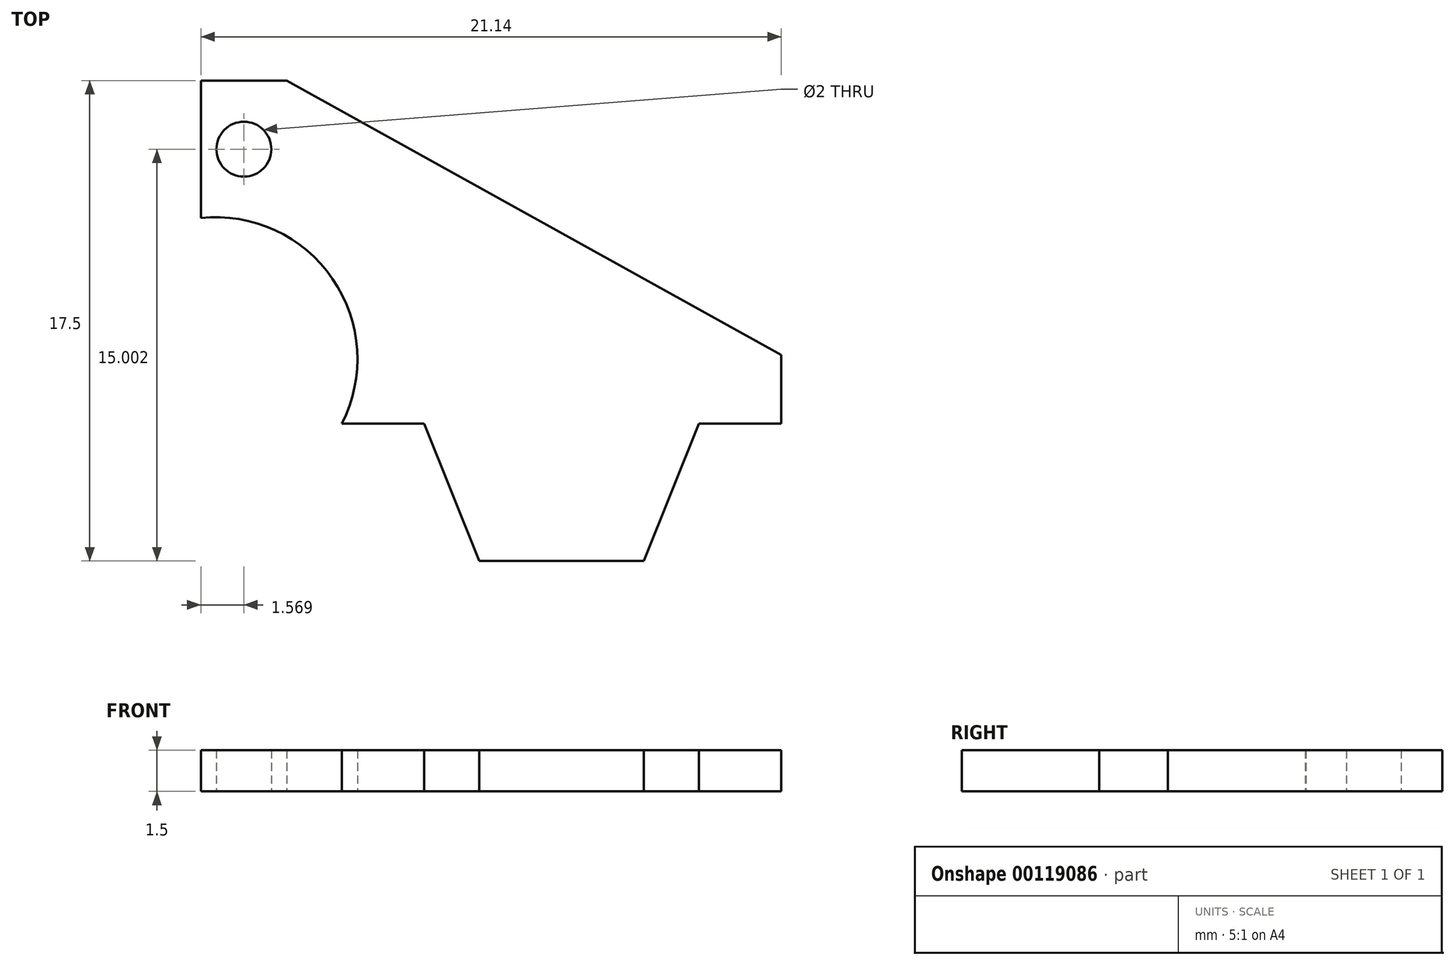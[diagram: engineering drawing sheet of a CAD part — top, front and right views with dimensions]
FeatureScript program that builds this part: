
annotation { "Feature Type Name" : "Feature", "Feature Type Description" : "" }
export const myFeature = defineFeature(function(context is Context, id is Id, definition is map)
    precondition{}
    {
        {
            var Q0;
            Q0=qCreatedBy(makeId("Top.planeOp"),FACE);
            var sketch = newSketch(context, id + "F0", { "sketchPlane" : qUnion([Q0])});
            skLineSegment(sketch, "E0", {"start": v(-58.9, 5.22) * mm, "end": v(-52.9, 5.22) * mm});
            skLineSegment(sketch, "E1", {"start": v(-55.9, 5.22) * mm, "end": v(-55.9, 10.22) * mm});
            skLineSegment(sketch, "E2", {"start": v(-55.9, 10.22) * mm, "end": v(-50.9, 10.22) * mm});
            skLineSegment(sketch, "E3", {"start": v(-55.9, 10.22) * mm, "end": v(-60.9, 10.22) * mm});
            skLineSegment(sketch, "E4", {"start": v(-60.9, 10.22) * mm, "end": v(-58.9, 5.22) * mm});
            skLineSegment(sketch, "E5", {"start": v(-52.9, 5.22) * mm, "end": v(-50.9, 10.22) * mm});
            skLineSegment(sketch, "E6", {"start": v(-60.9, 10.22) * mm, "end": v(-63.9, 10.22) * mm});
            skLineSegment(sketch, "E7", {"start": v(-50.9, 10.22) * mm, "end": v(-47.9, 10.22) * mm});
            skLineSegment(sketch, "E8", {"start": v(-47.9, 10.22) * mm, "end": v(-47.9, 12.72) * mm});
            skLineSegment(sketch, "E9", {"start": v(-58.9, 0) * mm, "end": v(-65.9, 0) * mm});
            skLineSegment(sketch, "E10", {"start": v(-58.9, 5.22) * mm, "end": v(-58.9, 22.72) * mm});
            skLineSegment(sketch, "E11", {"start": v(-65.9, 22.72) * mm, "end": v(-47.9, 12.72) * mm});
            skLineSegment(sketch, "E12", {"start": v(-65.9, 22.72) * mm, "end": v(-69.04, 22.72) * mm});
            skLineSegment(sketch, "E13", {"start": v(-69.04, 22.72) * mm, "end": v(-69.04, 17.72) * mm});
            skArc(sketch, "E14", {"start": v(-63.9, 10.22) * mm, "mid": v(-64.24, 15.5) * mm, "end": v(-69.04, 17.72) * mm});
            skCircle(sketch, "E15", {"center": v(-67.47, 20.22) * mm, "radius": 1 * mm});
            skPoint(sketch, "E15.centerSnap0", {"position": v(-69.04, 20.22) * mm});
            skPoint(sketch, "E15.centerSnap1", {"position": v(-67.47, 22.72) * mm});
            skSolve(sketch);
        }
        {
            var Q0;
            {var subQ6=sQuery(id+"F0.wireOp",EDGE,"E6");Q0=makeQuery(id+"F0.imprint","IMPRINT",FACE,{"disambiguationData":[TD([[makeQuery(id+"F0.imprint","IMPRINT",EDGE,{"derivedFrom":subQ6}),-1.0]])]});}
            var Q1;
            {var subQ1=sQuery(id+"F0.wireOp",EDGE,"E2");Q1=makeQuery(id+"F0.imprint","IMPRINT",FACE,{"disambiguationData":[TD([[makeQuery(id+"F0.imprint","IMPRINT",EDGE,{"derivedFrom":subQ1}),1.0]])]});}
            var Q2;
            {var subQ3=sQuery(id+"F0.wireOp",EDGE,"E1");Q2=makeQuery(id+"F0.imprint","IMPRINT",FACE,{"disambiguationData":[TD([[makeQuery(id+"F0.imprint","IMPRINT",EDGE,{"derivedFrom":subQ3}),1.0]])]});}
            var Q3;
            {var subQ0=sQuery(id+"F0.wireOp",EDGE,"E4");Q3=makeQuery(id+"F0.imprint","IMPRINT",FACE,{"disambiguationData":[TD([[makeQuery(id+"F0.imprint","IMPRINT",EDGE,{"derivedFrom":subQ0}),1.0]])]});}
            var Q4;
            {var subQ2=sQuery(id+"F0.wireOp",EDGE,"E1");Q4=makeQuery(id+"F0.imprint","IMPRINT",FACE,{"disambiguationData":[TD([[makeQuery(id+"F0.imprint","IMPRINT",EDGE,{"derivedFrom":subQ2}),-1.0]])]});}
            extrude(context, id + "F1", {"entities" : qUnion([Q0, Q1, Q2, Q3, Q4]), "depth" : 1.5 * mm});
        }
    });
